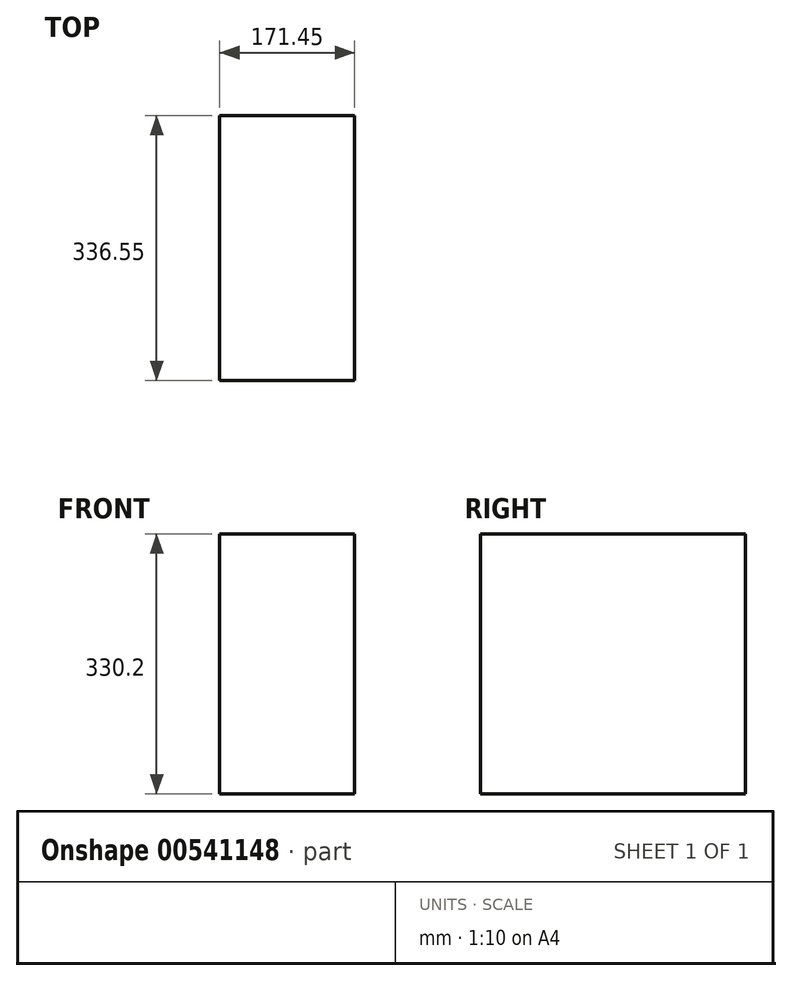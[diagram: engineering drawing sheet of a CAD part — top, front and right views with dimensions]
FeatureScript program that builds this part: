
annotation { "Feature Type Name" : "Feature", "Feature Type Description" : "" }
export const myFeature = defineFeature(function(context is Context, id is Id, definition is map)
    precondition{}
    {
        {
            var Q0;
            Q0=qCreatedBy(makeId("Top.planeOp"),FACE);
            var sketch = newSketch(context, id + "F0", { "sketchPlane" : qUnion([Q0])});
            skLineSegment(sketch, "E0.bottom", {"start": v(0, 0) * mm, "end": v(171.45, 0) * mm});
            skLineSegment(sketch, "E0.top", {"start": v(0, 336.55) * mm, "end": v(171.45, 336.55) * mm});
            skLineSegment(sketch, "E0.left", {"start": v(0, 0) * mm, "end": v(0, 336.55) * mm});
            skLineSegment(sketch, "E0.right", {"start": v(171.45, 0) * mm, "end": v(171.45, 336.55) * mm});
            skSolve(sketch);
        }
        {
            var Q0;
            Q0 = qSketchRegion(id + "F0", true);
            extrude(context, id + "F1", {"entities" : qUnion([Q0]), "depth" : 330.2 * mm, "offsetDistance" : 25.4 * mm});
        }
    });
